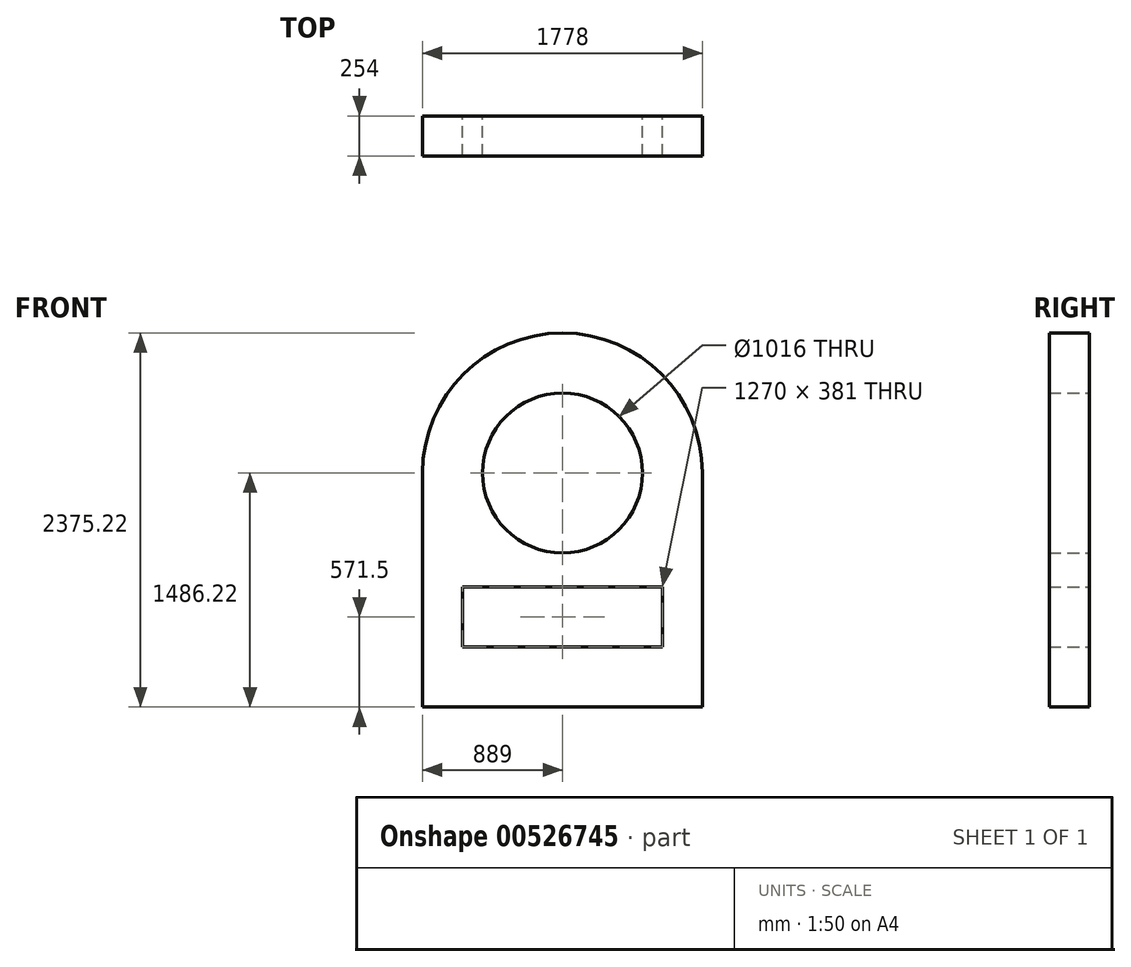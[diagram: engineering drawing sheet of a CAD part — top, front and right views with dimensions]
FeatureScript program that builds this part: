
annotation { "Feature Type Name" : "Feature", "Feature Type Description" : "" }
export const myFeature = defineFeature(function(context is Context, id is Id, definition is map)
    precondition{}
    {
        {
            var Q0;
            Q0=qCreatedBy(makeId("Front.planeOp"),FACE);
            var sketch = newSketch(context, id + "F0", { "sketchPlane" : qUnion([Q0])});
            skLineSegment(sketch, "E0", {"start": v(0, 0) * mm, "end": v(-1778, 0) * mm});
            skLineSegment(sketch, "E1", {"start": v(-1778, 0) * mm, "end": v(-1778, 1524) * mm});
            skLineSegment(sketch, "E2", {"start": v(0, 0) * mm, "end": v(0, 1524) * mm});
            skLineSegment(sketch, "E3", {"start": v(-1524, 762) * mm, "end": v(-1524, 381) * mm});
            skLineSegment(sketch, "E4", {"start": v(-1524, 381) * mm, "end": v(-254, 381) * mm});
            skLineSegment(sketch, "E5", {"start": v(-254, 381) * mm, "end": v(-254, 762) * mm});
            skLineSegment(sketch, "E6", {"start": v(-254, 762) * mm, "end": v(-1524, 762) * mm});
            skArc(sketch, "E7", {"start": v(0, 1486.22) * mm, "mid": v(-889, 2375.22) * mm, "end": v(-1778, 1486.22) * mm});
            skCircle(sketch, "E8", {"center": v(-889, 1486.22) * mm, "radius": 508 * mm});
            skSolve(sketch);
        }
        {
            var Q0;
            Q0 = qSketchRegion(id + "F0", true);
            extrude(context, id + "F1", {"entities" : qUnion([Q0]), "depth" : 254 * mm, "offsetDistance" : 25.4 * mm});
        }
    });
